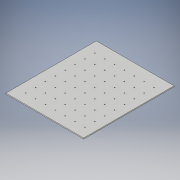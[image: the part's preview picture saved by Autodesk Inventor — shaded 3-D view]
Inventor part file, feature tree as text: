
AUTODESK INVENTOR PART (.ipt)
format: ipt  version: 2018 (Build 220112000, 112)  size: 224,768 bytes
history: native  units: in
note: dims shown in document units (in); Inventor stores cm internally (conversion verified against a paired STEP export)
features: extrude x2, sketch x2
ambient origin geometry x8: Origin, YZ Plane, XZ Plane, XY Plane, X Axis, Y Axis, Z Axis, Center Point
bodies: Solid1 (feature_tree)
feature tree (4):
  extrude  "Extrusion1"  Depth=18.3in
  extrude  "Extrusion2"  Depth=0.2in
  sketch  "Sketch1"  dims[d0=15.748in d1=18.3in]
  sketch  "Sketch2"  dims[d2=0.2in d3=0.0in d4=0.164in d5=0.164in d6=0.164in d7=0.164in d8=0.164in d9=0.164in d10=0.164in d11=0.164in d12=0.164in d13=0.164in d14=0.164in d15=0.164in d16=0.164in d17=0.164in d18=0.164in d19=0.164in d20=0.164in d21=0.164in d22=0.164in d23=0.164in d24=0.164in d25=0.164in d26=0.164in d27=0.164in d28=0.164in d29=0.164in d30=0.164in d31=0.164in d32=0.164in d33=0.164in d34=0.164in d35=0.164in d36=0.164in d37=0.164in d38=0.164in d39=0.164in d40=0.164in d41=0.164in d42=0.164in d43=0.164in d44=0.164in d45=0.164in d46=0.164in d47=0.164in d48=0.164in d49=0.164in d50=0.164in d51=0.164in d52=0.164in d53=0.164in d54=0.164in d55=0.164in d56=0.164in d57=0.164in d58=0.164in d59=0.164in d60=0.0in d61=0.0in]
